FCSTD DOCUMENT  (FreeCAD 0.14R3703 (Git))
Label: hullBowFC
License: CC-BY 3.0
LicenseURL: http://creativecommons.org/licenses/by/3.0/
objects: Sketcher::SketchObject×7
note: 7 computed .brp shape members not serialized (recipe doc carries the construction recipe); baked Part::Feature solids carry a one-line shape summary decoded from their .brp

FEATURE [Sketcher::SketchObject] Sketch  label="stemline"
  Placement = pos=(0,0,0) rot=(0.57735,0.57735,0.57735;2.0944rad)
  sketch-geometry (3):
    g0: LineSegment StartX=0 StartY=0 StartZ=0 EndX=13.3299 EndY=17.0878 EndZ=0
    g1: LineSegment StartX=13.3299 StartY=17.0878 StartZ=0 EndX=29.7111 EndY=33.469 EndZ=0
    g2: LineSegment StartX=29.7111 StartY=33.469 StartZ=0 EndX=52.7022 EndY=46.4016 EndZ=0
  constraints (2):
    c: Coincident(g0,g1)
    c: Coincident(g1,g2)
FEATURE [Sketcher::SketchObject] Sketch001  label="cs1"
  Placement = pos=(0,0,0) rot=(1,0,0;1.5708rad)
  sketch-geometry (3):
    g0: LineSegment StartX=0 StartY=0 StartZ=0 EndX=12.1501 EndY=10.5555 EndZ=0
    g1: LineSegment StartX=12.1501 StartY=10.5555 StartZ=0 EndX=20.6417 EndY=24.5851 EndZ=0
    g2: LineSegment StartX=20.6417 StartY=24.5851 StartZ=0 EndX=26.1797 EndY=46.7372 EndZ=0
  constraints (2):
    c: Coincident(g0,g1)
    c: Coincident(g1,g2)
FEATURE [Sketcher::SketchObject] Sketch002  label="cs2"
  Placement = pos=(0,-20,0) rot=(1,0,0;1.5708rad)
  sketch-geometry (3):
    g0: LineSegment StartX=0 StartY=0 StartZ=0 EndX=18.7957 EndY=8.34027 EndZ=0
    g1: LineSegment StartX=18.7957 StartY=8.34027 StartZ=0 EndX=30.9794 EndY=23.8467 EndZ=0
    g2: LineSegment StartX=30.9794 StartY=23.8467 StartZ=0 EndX=36.5174 EndY=46.368 EndZ=0
  constraints (2):
    c: Coincident(g0,g1)
    c: Coincident(g1,g2)
FEATURE [Sketcher::SketchObject] Sketch004  label="transomXY"
  Placement = pos=(0,-60,0) rot=(0,0,1;0rad)
  sketch-geometry (3):
    g0: LineSegment StartX=-0.069336 StartY=-20.4675 StartZ=0 EndX=25.0103 EndY=-20.3102 EndZ=0
    g1: LineSegment StartX=25.0103 StartY=-20.3102 StartZ=0 EndX=38.297 EndY=-20.2316 EndZ=0
    g2: LineSegment StartX=38.297 StartY=-20.2316 StartZ=0 EndX=44.3064 EndY=-20.1146 EndZ=0
  constraints (2):
    c: Coincident(g0,g1)
    c: Coincident(g1,g2)
FEATURE [Sketcher::SketchObject] Sketch005  label="cs3"
  Placement = pos=(0,-40,0) rot=(1,0,0;1.5708rad)
  sketch-geometry (3):
    g0: LineSegment StartX=0 StartY=0 StartZ=0 EndX=25.0073 EndY=8.15455 EndZ=0
    g1: LineSegment StartX=25.0073 StartY=8.15455 StartZ=0 EndX=38.3264 EndY=24.1918 EndZ=0
    g2: LineSegment StartX=38.3264 StartY=24.1918 StartZ=0 EndX=43.5322 EndY=45.2604 EndZ=0
  constraints (2):
    c: Coincident(g0,g1)
    c: Coincident(g1,g2)
FEATURE [Sketcher::SketchObject] Sketch006  label="cs4"
  Placement = pos=(0,-60,0) rot=(1,0,0;1.5708rad)
  sketch-geometry (3):
    g0: LineSegment StartX=0 StartY=0 StartZ=0 EndX=25.0073 EndY=8.15455 EndZ=0
    g1: LineSegment StartX=25.0073 StartY=8.15455 StartZ=0 EndX=38.3264 EndY=24.1918 EndZ=0
    g2: LineSegment StartX=38.3264 StartY=24.1918 StartZ=0 EndX=44.2706 EndY=45.9988 EndZ=0
  constraints (2):
    c: Coincident(g0,g1)
    c: Coincident(g1,g2)
FEATURE [Sketcher::SketchObject] Sketch007  label="cs5"
  Placement = pos=(0,-80,0) rot=(1,0,0;1.5708rad)
  sketch-geometry (3):
    g0: LineSegment StartX=0 StartY=0 StartZ=0 EndX=25.0073 EndY=8.15455 EndZ=0
    g1: LineSegment StartX=25.0073 StartY=8.15455 StartZ=0 EndX=38.3264 EndY=24.1918 EndZ=0
    g2: LineSegment StartX=38.3264 StartY=24.1918 StartZ=0 EndX=44.2706 EndY=45.6296 EndZ=0
  constraints (2):
    c: Coincident(g0,g1)
    c: Coincident(g1,g2)
